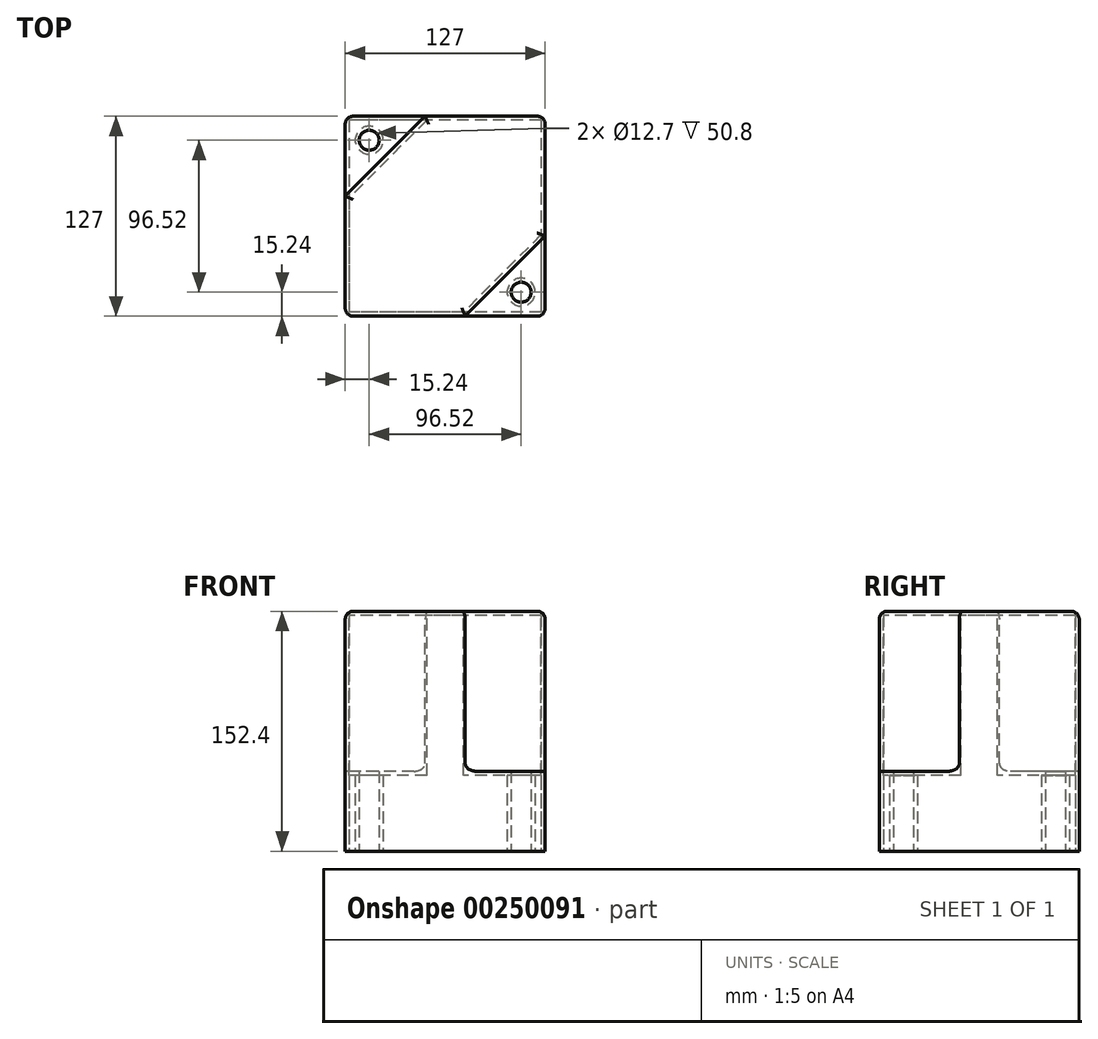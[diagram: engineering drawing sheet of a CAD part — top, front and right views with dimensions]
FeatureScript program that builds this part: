
annotation { "Feature Type Name" : "Feature", "Feature Type Description" : "" }
export const myFeature = defineFeature(function(context is Context, id is Id, definition is map)
    precondition{}
    {
        {
            var Q0;
            Q0=qCreatedBy(makeId("Top.planeOp"),FACE);
            var sketch = newSketch(context, id + "F0", { "sketchPlane" : qUnion([Q0])});
            skLineSegment(sketch, "E0.bottom", {"start": v(63.5, 63.5) * mm, "end": v(-63.5, 63.5) * mm});
            skLineSegment(sketch, "E0.top", {"start": v(63.5, -63.5) * mm, "end": v(-63.5, -63.5) * mm});
            skLineSegment(sketch, "E0.left", {"start": v(63.5, 63.5) * mm, "end": v(63.5, -63.5) * mm});
            skLineSegment(sketch, "E0.right", {"start": v(-63.5, 63.5) * mm, "end": v(-63.5, -63.5) * mm});
            skPoint(sketch, "E0.middle", {"position": v(0, 0) * mm});
            skSolve(sketch);
        }
        {
            var Q0;
            Q0 = qSketchRegion(id + "F0", true);
            extrude(context, id + "F1", {"entities" : qUnion([Q0]), "depth" : 152.4 * mm});
        }
        {
            var Q0;
            Q0=makeQuery(id+"F1.opExtrude","CAP_FACE",FACE,{"disambiguationData":[OSD([sQuery(id+"F0.wireOp",EDGE,"E0.bottom"),sQuery(id+"F0.wireOp",EDGE,"E0.top"),sQuery(id+"F0.wireOp",EDGE,"E0.left"),sQuery(id+"F0.wireOp",EDGE,"E0.right")])],"isStart":false});
            var sketch = newSketch(context, id + "F2", { "sketchPlane" : qUnion([Q0])});
            skLineSegment(sketch, "E1", {"start": v(-12.7, 63.5) * mm, "end": v(-63.5, 12.7) * mm});
            skLineSegment(sketch, "E2", {"start": v(-63.5, 12.7) * mm, "end": v(-63.5, 63.5) * mm});
            skLineSegment(sketch, "E3", {"start": v(-63.5, 63.5) * mm, "end": v(-12.7, 63.5) * mm});
            skLineSegment(sketch, "E4", {"start": v(63.5, -63.5) * mm, "end": v(63.5, -12.7) * mm});
            skLineSegment(sketch, "E5", {"start": v(63.5, -12.7) * mm, "end": v(12.7, -63.5) * mm});
            skLineSegment(sketch, "E6", {"start": v(12.7, -63.5) * mm, "end": v(63.5, -63.5) * mm});
            skSolve(sketch);
        }
        {
            var Q0;
            Q0 = qSketchRegion(id + "F2", true);
            extrude(context, id + "F3", {"entities" : qUnion([Q0]), "operationType" : NewBodyOperationType.REMOVE, "oppositeDirection" : true, "depth" : 101.6 * mm});
        }
        {
            var Q0;
            Q0=qCreatedBy(makeId("Top.planeOp"),FACE);
            var sketch = newSketch(context, id + "F4", { "sketchPlane" : qUnion([Q0])});
            skCircle(sketch, "E7", {"center": v(-48.26, 48.26) * mm, "radius": 6.35 * mm});
            skCircle(sketch, "E8", {"center": v(48.26, -48.26) * mm, "radius": 6.35 * mm});
            skSolve(sketch);
        }
        {
            var Q0;
            Q0 = qSketchRegion(id + "F4", true);
            extrude(context, id + "F5", {"entities" : qUnion([Q0]), "operationType" : NewBodyOperationType.REMOVE, "depth" : 203.2 * mm});
        }
        {
            var Q0;
            Q0=makeQuery(id+"F1.opExtrude","CAP_FACE",FACE,{"disambiguationData":[OSD([sQuery(id+"F0.wireOp",EDGE,"E0.bottom"),sQuery(id+"F0.wireOp",EDGE,"E0.top"),sQuery(id+"F0.wireOp",EDGE,"E0.left"),sQuery(id+"F0.wireOp",EDGE,"E0.right")])],"isStart":true});
            shell(context, id + "F6", {"entities" : qUnion([Q0]), "thickness" : 2.54 * mm});
        }
        {
            var Q0;
            Q0=makeQuery(id+"F1.opExtrude","CAP_FACE",FACE,{"disambiguationData":[OSD([sQuery(id+"F0.wireOp",EDGE,"E0.bottom"),sQuery(id+"F0.wireOp",EDGE,"E0.top"),sQuery(id+"F0.wireOp",EDGE,"E0.left"),sQuery(id+"F0.wireOp",EDGE,"E0.right")])],"isStart":false});
            var Q1;
            Q1=makeQuery(id+"F3.boolean.opBoolean","COPY",EDGE,{"derivedFrom":makeQuery(id+"F3.opExtrude","CAP_EDGE",EDGE,{"disambiguationData":[OSD([sQuery(id+"F2.wireOp",EDGE,"E5")])],"isStart":false})});
            var Q2;
            Q2=makeQuery(id+"F3.boolean.opBoolean","COPY",EDGE,{"derivedFrom":makeQuery(id+"F3.opExtrude","SWEPT_EDGE",EDGE,{"disambiguationData":[OSD([sQuery(id+"F0.wireOp",EDGE,"E0.left"),sQuery(id+"F2.wireOp",EDGE,"E4"),sQuery(id+"F2.wireOp",EDGE,"E5")])]})});
            var Q3;
            Q3=makeQuery(id+"F3.boolean.opBoolean","COPY",EDGE,{"derivedFrom":makeQuery(id+"F3.opExtrude","SWEPT_EDGE",EDGE,{"disambiguationData":[OSD([sQuery(id+"F0.wireOp",EDGE,"E0.top"),sQuery(id+"F2.wireOp",EDGE,"E5"),sQuery(id+"F2.wireOp",EDGE,"E6")])]})});
            var Q4;
            Q4=makeQuery(id+"F1.opExtrude","SWEPT_EDGE",EDGE,{"disambiguationData":[OSD([sQuery(id+"F0.wireOp",EDGE,"E0.top"),sQuery(id+"F0.wireOp",EDGE,"E0.left")])]});
            var Q5;
            Q5=makeQuery(id+"F1.opExtrude","SWEPT_EDGE",EDGE,{"disambiguationData":[OSD([sQuery(id+"F0.wireOp",EDGE,"E0.top"),sQuery(id+"F0.wireOp",EDGE,"E0.right")])]});
            var Q6;
            Q6=makeQuery(id+"F1.opExtrude","SWEPT_EDGE",EDGE,{"disambiguationData":[OSD([sQuery(id+"F0.wireOp",EDGE,"E0.bottom"),sQuery(id+"F0.wireOp",EDGE,"E0.left")])]});
            var Q7;
            Q7=makeQuery(id+"F3.boolean.opBoolean","COPY",EDGE,{"derivedFrom":makeQuery(id+"F3.opExtrude","SWEPT_EDGE",EDGE,{"disambiguationData":[OSD([sQuery(id+"F0.wireOp",EDGE,"E0.bottom"),sQuery(id+"F2.wireOp",EDGE,"E1"),sQuery(id+"F2.wireOp",EDGE,"E3")])]})});
            var Q8;
            Q8=makeQuery(id+"F3.boolean.opBoolean","COPY",EDGE,{"derivedFrom":makeQuery(id+"F3.opExtrude","SWEPT_EDGE",EDGE,{"disambiguationData":[OSD([sQuery(id+"F0.wireOp",EDGE,"E0.right"),sQuery(id+"F2.wireOp",EDGE,"E1"),sQuery(id+"F2.wireOp",EDGE,"E2")])]})});
            var Q9;
            Q9=makeQuery(id+"F3.boolean.opBoolean","COPY",EDGE,{"derivedFrom":makeQuery(id+"F3.opExtrude","CAP_EDGE",EDGE,{"disambiguationData":[OSD([sQuery(id+"F2.wireOp",EDGE,"E1")])],"isStart":false})});
            var Q10;
            Q10=makeQuery(id+"F3.boolean.opBoolean","COPY",EDGE,{"derivedFrom":makeQuery(id+"F3.opExtrude","CAP_EDGE",EDGE,{"disambiguationData":[OSD([sQuery(id+"F2.wireOp",EDGE,"E2")])],"isStart":false})});
            var Q11;
            Q11=makeQuery(id+"F1.opExtrude","SWEPT_EDGE",EDGE,{"disambiguationData":[OSD([sQuery(id+"F0.wireOp",EDGE,"E0.bottom"),sQuery(id+"F0.wireOp",EDGE,"E0.right")])]});
            fillet(context, id + "F7", {"entities" : qUnion([Q0, Q1, Q2, Q3, Q4, Q5, Q6, Q7, Q8, Q9, Q10, Q11]), "radius" : 5.08 * mm, "tangentPropagation" : true, "allowEdgeOverflow" : false});
        }
    });
